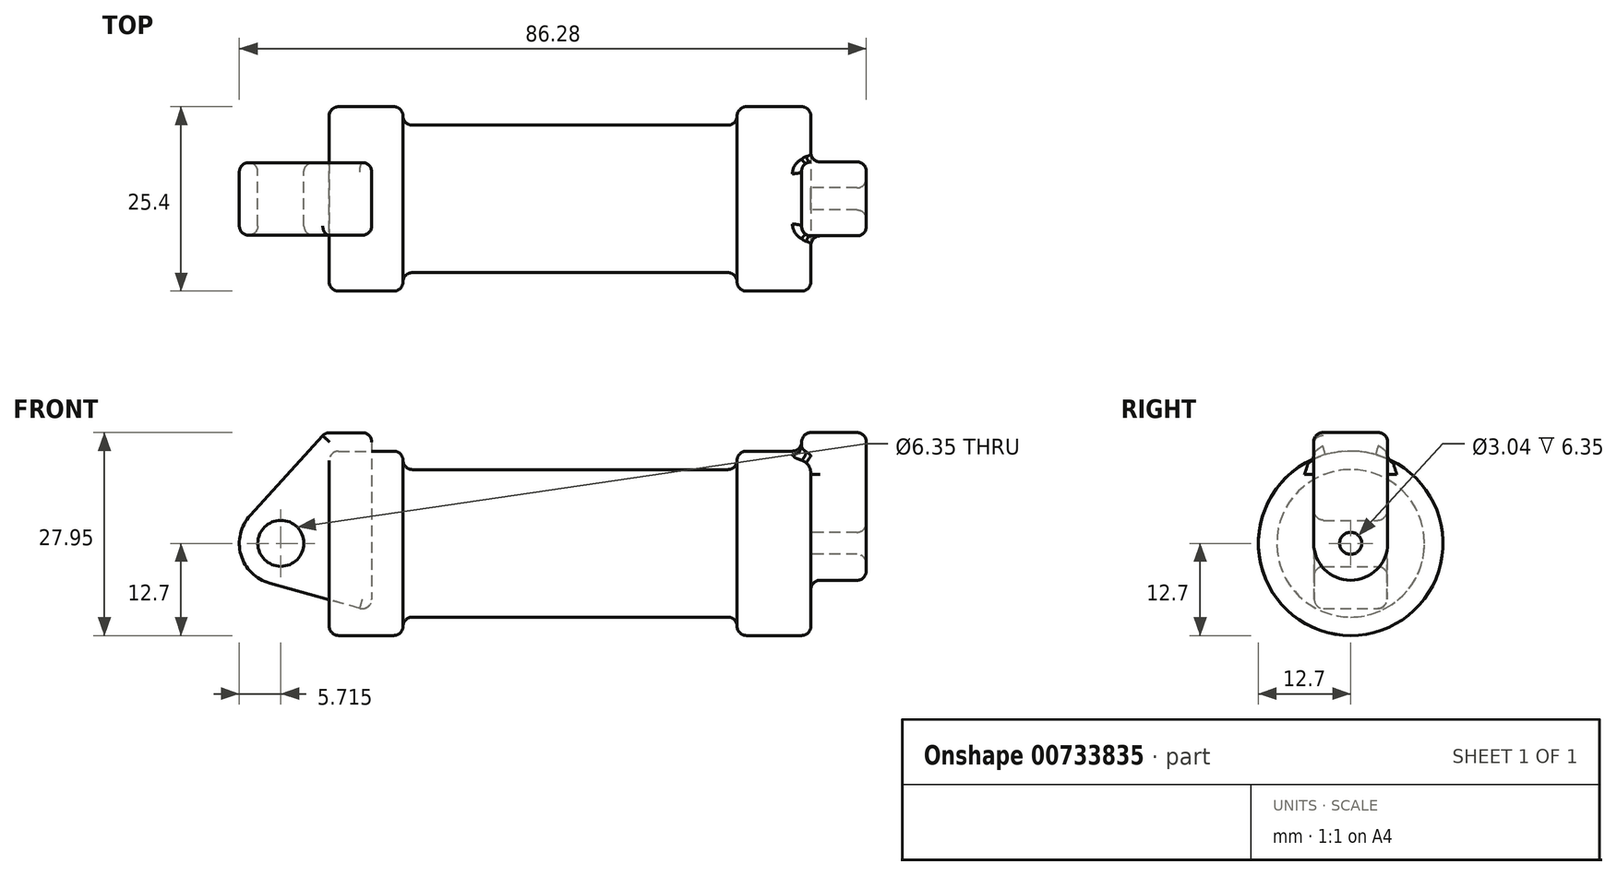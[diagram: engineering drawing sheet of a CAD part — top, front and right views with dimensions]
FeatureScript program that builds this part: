
annotation { "Feature Type Name" : "Feature", "Feature Type Description" : "" }
export const myFeature = defineFeature(function(context is Context, id is Id, definition is map)
    precondition{}
    {
        {
            var Q0;
            Q0=qCreatedBy(makeId("Front.planeOp"),FACE);
            var sketch = newSketch(context, id + "F0", { "sketchPlane" : qUnion([Q0])});
            skLineSegment(sketch, "E0", {"start": v(0, 0) * mm, "end": v(0, 12.7) * mm});
            skLineSegment(sketch, "E1", {"start": v(0, 12.7) * mm, "end": v(10.16, 12.7) * mm});
            skLineSegment(sketch, "E2", {"start": v(10.16, 12.7) * mm, "end": v(10.16, 10.16) * mm});
            skLineSegment(sketch, "E3", {"start": v(10.16, 10.16) * mm, "end": v(56.13, 10.16) * mm});
            skLineSegment(sketch, "E4", {"start": v(56.13, 10.16) * mm, "end": v(56.13, 12.7) * mm});
            skLineSegment(sketch, "E5", {"start": v(56.13, 12.7) * mm, "end": v(66.3, 12.7) * mm});
            skLineSegment(sketch, "E6", {"start": v(66.3, 12.7) * mm, "end": v(66.3, 0) * mm});
            skLineSegment(sketch, "E7", {"start": v(66.3, 0) * mm, "end": v(0, 0) * mm});
            skLineSegment(sketch, "E8", {"start": v(5.84, 15.24) * mm, "end": v(-0.5, 15.24) * mm});
            skLineSegment(sketch, "E9", {"start": v(-0.5, 15.24) * mm, "end": v(-10.88, 3.85) * mm});
            skLineSegment(sketch, "E10", {"start": v(0, 0) * mm, "end": v(-6.65, 0) * mm});
            skCircle(sketch, "E11", {"center": v(-6.65, 0) * mm, "radius": 5.72 * mm});
            skCircle(sketch, "E12", {"center": v(-6.65, 0) * mm, "radius": 3.18 * mm});
            skLineSegment(sketch, "E13", {"start": v(5.84, 15.24) * mm, "end": v(5.84, -9.4) * mm});
            skLineSegment(sketch, "E14", {"start": v(5.84, -9.4) * mm, "end": v(-8.18, -5.5) * mm});
            skSolve(sketch);
        }
        {
            var Q0;
            {var subQ0=sQuery(id+"F0.wireOp",EDGE,"E2");Q0=makeQuery(id+"F0.imprint","IMPRINT",FACE,{"disambiguationData":[TD([[makeQuery(id+"F0.imprint","IMPRINT",EDGE,{"derivedFrom":subQ0}),-1.0]])]});}
            var Q1;
            {var subQ0=sQuery(id+"F0.wireOp",EDGE,"E0");Q1=makeQuery(id+"F0.imprint","IMPRINT",FACE,{"disambiguationData":[TD([[makeQuery(id+"F0.imprint","IMPRINT",EDGE,{"derivedFrom":subQ0}),-1.0]])]});}
            var Q2;
            Q2=sQuery(id+"F0.wireOp",EDGE,"E7");
            revolve(context, id + "F1", {"surfaceOperationType" : NewSurfaceOperationType.NEW, "entities" : qUnion([Q0, Q1]), "axis" : qUnion([Q2]), "revolveType" : RevolveType.FULL});
        }
        {
            var Q0;
            {var subQ1=sQuery(id+"F0.wireOp",EDGE,"E0");Q0=makeQuery(id+"F0.imprint","IMPRINT",FACE,{"disambiguationData":[TD([[makeQuery(id+"F0.imprint","IMPRINT",EDGE,{"derivedFrom":subQ1}),1.0]])]});}
            var Q1;
            {var subQ0=sQuery(id+"F0.wireOp",EDGE,"E14");Q1=makeQuery(id+"F0.imprint","IMPRINT",FACE,{"disambiguationData":[TD([[makeQuery(id+"F0.imprint","IMPRINT",EDGE,{"derivedFrom":subQ0}),-1.0]])]});}
            var Q2;
            {var subQ5=sQuery(id+"F0.wireOp",EDGE,"E12");Q2=makeQuery(id+"F0.imprint","IMPRINT",FACE,{"disambiguationData":[TD([[makeQuery(id+"F0.imprint","IMPRINT",EDGE,{"derivedFrom":subQ5}),-1.0]])]});}
            var Q3;
            {var subQ0=sQuery(id+"F0.wireOp",EDGE,"E0");Q3=makeQuery(id+"F0.imprint","IMPRINT",FACE,{"disambiguationData":[TD([[makeQuery(id+"F0.imprint","IMPRINT",EDGE,{"derivedFrom":subQ0}),-1.0]])]});}
            extrude(context, id + "F2", {"entities" : qUnion([Q0, Q1, Q2, Q3]), "endBound" : BoundingType.SYMMETRIC, "depth" : 10 * mm, "offsetDistance" : 25.4 * mm, "hasSecondDirection" : true, "secondDirectionOppositeDirection" : true, "secondDirectionDepth" : 50.8 * mm});
        }
        {
            var Q0;
            Q0=makeQuery(id+"F1.opRevolve","SWEPT_FACE",FACE,{"disambiguationData":[OSD([sQuery(id+"F0.wireOp",EDGE,"E6")])]});
            var sketch = newSketch(context, id + "F3", { "sketchPlane" : qUnion([Q0])});
            skCircle(sketch, "E15", {"center": v(0, 0) * mm, "radius": 1.52 * mm});
            skCircle(sketch, "E16", {"center": v(0, 0) * mm, "radius": 5.1 * mm});
            skLineSegment(sketch, "E17", {"start": v(-5.1, 0) * mm, "end": v(-5.1, 15.25) * mm});
            skLineSegment(sketch, "E18", {"start": v(-5.1, 15.25) * mm, "end": v(5.08, 15.25) * mm});
            skLineSegment(sketch, "E19", {"start": v(5.08, 15.25) * mm, "end": v(5.1, 0) * mm});
            skSolve(sketch);
        }
        {
            var Q0;
            Q0 = qSketchRegion(id + "F3", true);
            extrude(context, id + "F4", {"entities" : qUnion([Q0]), "operationType" : NewBodyOperationType.ADD, "depth" : 7.62 * mm, "offsetDistance" : 25.4 * mm, "hasSecondDirection" : true, "secondDirectionOppositeDirection" : true, "secondDirectionDepth" : 1.27 * mm});
        }
        {
            var Q0;
            Q0=makeQuery(id+"F2.opExtrude","CAP_EDGE",EDGE,{"disambiguationData":[OSD([sQuery(id+"F0.wireOp",EDGE,"E8")])],"isStart":true});
            var Q1;
            Q1=makeQuery(id+"F2.opExtrude","CAP_EDGE",EDGE,{"disambiguationData":[OSD([sQuery(id+"F0.wireOp",EDGE,"E13")])],"isStart":true});
            var Q2;
            Q2=makeQuery(id+"F2.opExtrude","CAP_EDGE",EDGE,{"disambiguationData":[OSD([sQuery(id+"F0.wireOp",EDGE,"E9")])],"isStart":true});
            var Q3;
            Q3=makeQuery(id+"F2.opExtrude","CAP_EDGE",EDGE,{"disambiguationData":[OSD([sQuery(id+"F0.wireOp",EDGE,"E11")])],"isStart":false});
            var Q4;
            Q4=makeQuery(id+"F2.opExtrude","CAP_EDGE",EDGE,{"disambiguationData":[OSD([sQuery(id+"F0.wireOp",EDGE,"E12")])],"isStart":false});
            var Q5;
            Q5=makeQuery(id+"F2.opExtrude","CAP_EDGE",EDGE,{"disambiguationData":[OSD([sQuery(id+"F0.wireOp",EDGE,"E12")])],"isStart":true});
            var Q6;
            Q6=makeQuery(id+"F2.opExtrude","SWEPT_EDGE",EDGE,{"disambiguationData":[OSD([sQuery(id+"F0.wireOp",EDGE,"E8"),sQuery(id+"F0.wireOp",EDGE,"E13")])]});
            var Q7;
            Q7=makeQuery(id+"F2.opExtrude","SWEPT_EDGE",EDGE,{"disambiguationData":[OSD([sQuery(id+"F0.wireOp",EDGE,"E8"),sQuery(id+"F0.wireOp",EDGE,"E9")])]});
            fillet(context, id + "F5", {"entities" : qUnion([Q0, Q1, Q2, Q3, Q4, Q5, Q6, Q7]), "radius" : 1.27 * mm, "tangentPropagation" : true, "allowEdgeOverflow" : false});
        }
        {
            var Q0;
            Q0=makeQuery(id+"F1.opRevolve","SWEPT_EDGE",EDGE,{"disambiguationData":[OSD([sQuery(id+"F0.wireOp",EDGE,"E3"),sQuery(id+"F0.wireOp",EDGE,"E4")])]});
            var Q1;
            Q1=makeQuery(id+"F1.opRevolve","SWEPT_EDGE",EDGE,{"disambiguationData":[OSD([sQuery(id+"F0.wireOp",EDGE,"E5"),sQuery(id+"F0.wireOp",EDGE,"E6")])]});
            var Q2;
            Q2=makeQuery(id+"F1.opRevolve","SWEPT_EDGE",EDGE,{"disambiguationData":[OSD([sQuery(id+"F0.wireOp",EDGE,"E4"),sQuery(id+"F0.wireOp",EDGE,"E5")])]});
            fillet(context, id + "F6", {"entities" : qUnion([Q0, Q1, Q2]), "radius" : 1.27 * mm, "tangentPropagation" : true, "allowEdgeOverflow" : false});
        }
        {
            var Q0;
            Q0=makeQuery(id+"F1.opRevolve","SWEPT_EDGE",EDGE,{"disambiguationData":[OSD([sQuery(id+"F0.wireOp",EDGE,"E2"),sQuery(id+"F0.wireOp",EDGE,"E3")])]});
            var Q1;
            Q1=makeQuery(id+"F1.opRevolve","SWEPT_EDGE",EDGE,{"disambiguationData":[OSD([sQuery(id+"F0.wireOp",EDGE,"E1"),sQuery(id+"F0.wireOp",EDGE,"E2")])]});
            var Q2;
            Q2=makeQuery(id+"F1.opRevolve","SWEPT_EDGE",EDGE,{"disambiguationData":[OSD([sQuery(id+"F0.wireOp",EDGE,"E0"),sQuery(id+"F0.wireOp",EDGE,"E1")])]});
            fillet(context, id + "F7", {"entities" : qUnion([Q0, Q1, Q2]), "radius" : 1.27 * mm, "tangentPropagation" : true, "allowEdgeOverflow" : false});
        }
        {
            var Q0;
            Q0=makeQuery(id+"F4.opExtrude","SWEPT_EDGE",EDGE,{"disambiguationData":[OSD([sQuery(id+"F3.wireOp",EDGE,"E18"),sQuery(id+"F3.wireOp",EDGE,"E19")])]});
            var Q1;
            Q1=makeQuery(id+"F4.opExtrude","CAP_EDGE",EDGE,{"disambiguationData":[OSD([sQuery(id+"F3.wireOp",EDGE,"E19")])],"isStart":false});
            var Q2;
            Q2=makeQuery(id+"F4.boolean.opBoolean","INTERSECT",EDGE,{"derivedFrom":[makeQuery(id+"F1.opRevolve","SWEPT_FACE",FACE,{"disambiguationData":[OSD([sQuery(id+"F0.wireOp",EDGE,"E6")])]}),makeQuery(id+"F4.opExtrude","SWEPT_FACE",FACE,{"disambiguationData":[OSD([sQuery(id+"F3.wireOp",EDGE,"E16")])]})]});
            var Q3;
            Q3=makeQuery(id+"F4.opExtrude","SWEPT_FACE",FACE,{"disambiguationData":[OSD([sQuery(id+"F3.wireOp",EDGE,"E18")])]});
            var Q4;
            Q4=makeQuery(id+"F4.opExtrude","CAP_FACE",FACE,{"disambiguationData":[OSD([sQuery(id+"F3.wireOp",EDGE,"E15"),sQuery(id+"F3.wireOp",EDGE,"E16"),sQuery(id+"F3.wireOp",EDGE,"E17"),sQuery(id+"F3.wireOp",EDGE,"E18"),sQuery(id+"F3.wireOp",EDGE,"E19")])],"isStart":true});
            fillet(context, id + "F8", {"entities" : qUnion([Q0, Q1, Q2, Q3, Q4]), "radius" : 1.27 * mm, "tangentPropagation" : true, "allowEdgeOverflow" : false});
        }
        {
            var Q0;
            Q0=makeQuery(id+"F2.opExtrude","CAP_FACE",FACE,{"disambiguationData":[OSD([sQuery(id+"F0.wireOp",EDGE,"E8"),sQuery(id+"F0.wireOp",EDGE,"E9"),sQuery(id+"F0.wireOp",EDGE,"E11"),sQuery(id+"F0.wireOp",EDGE,"E12"),sQuery(id+"F0.wireOp",EDGE,"E13"),sQuery(id+"F0.wireOp",EDGE,"E14")])],"isStart":false});
            var Q1;
            Q1=makeQuery(id+"F2.opExtrude","SWEPT_FACE",FACE,{"disambiguationData":[OSD([sQuery(id+"F0.wireOp",EDGE,"E13")])]});
            var Q2;
            Q2=makeQuery(id+"F4.opExtrude","CAP_EDGE",EDGE,{"disambiguationData":[OSD([sQuery(id+"F3.wireOp",EDGE,"E15")])],"isStart":false});
            fillet(context, id + "F9", {"entities" : qUnion([Q0, Q1, Q2]), "radius" : 1.27 * mm, "tangentPropagation" : true, "allowEdgeOverflow" : false});
        }
    });
